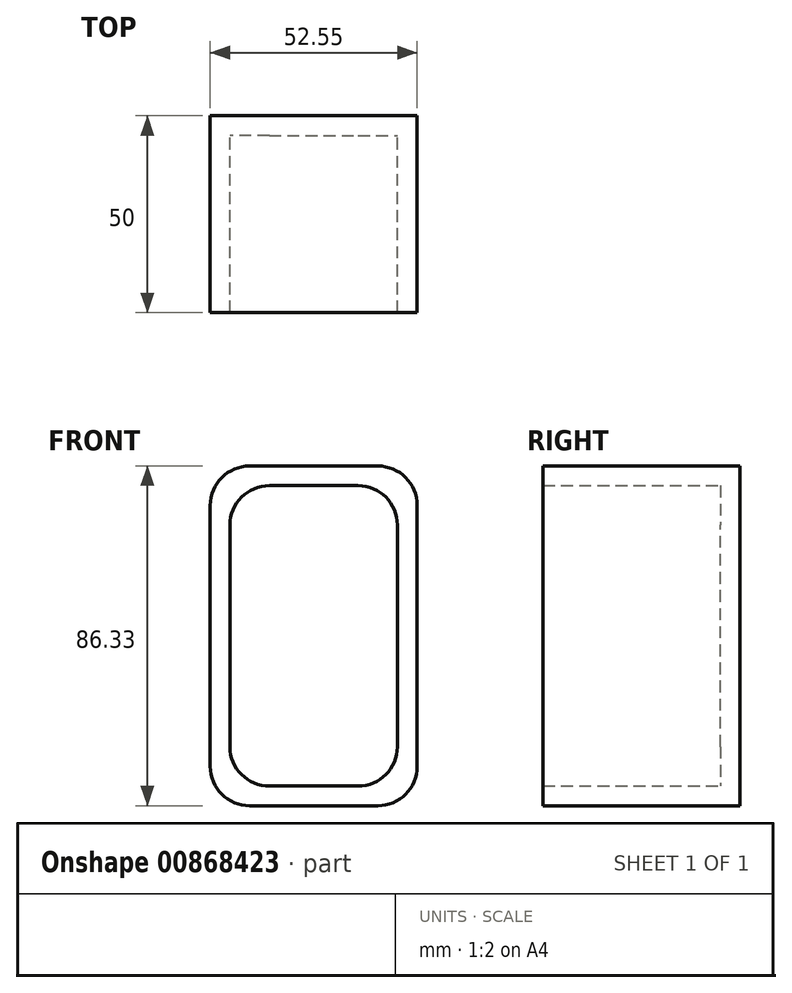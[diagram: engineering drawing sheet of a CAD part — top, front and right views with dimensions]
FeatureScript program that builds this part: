
annotation { "Feature Type Name" : "Feature", "Feature Type Description" : "" }
export const myFeature = defineFeature(function(context is Context, id is Id, definition is map)
    precondition{}
    {
        {
            var Q0;
            Q0=qCreatedBy(makeId("Front.planeOp"),FACE);
            var sketch = newSketch(context, id + "F0", { "sketchPlane" : qUnion([Q0])});
            skLineSegment(sketch, "E0.bottom", {"start": v(0, 0) * mm, "end": v(52.55, 0) * mm});
            skLineSegment(sketch, "E0.top", {"start": v(0, 51.33) * mm, "end": v(52.55, 51.33) * mm});
            skLineSegment(sketch, "E0.left", {"start": v(0, 0) * mm, "end": v(0, 51.33) * mm});
            skLineSegment(sketch, "E0.right", {"start": v(52.55, 0) * mm, "end": v(52.55, 51.33) * mm});
            skSolve(sketch);
        }
        {
            var Q0;
            Q0=makeQuery(id+"F0.imprint","IMPRINT",FACE,{"disambiguationData":[TD([[makeQuery(id+"F0.imprint","IMPRINT",EDGE,{"derivedFrom":sQuery(id+"F0.wireOp",EDGE,"E0.bottom")}),1.0]])]});
            extrude(context, id + "F1", {"entities" : qUnion([Q0]), "depth" : 50 * mm, "offsetDistance" : 25 * mm});
        }
        {
            var Q0;
            Q0=makeQuery(id+"F1.opExtrude","SWEPT_FACE",FACE,{"disambiguationData":[OSD([sQuery(id+"F0.wireOp",EDGE,"E0.top")])]});
            extrude(context, id + "F2", {"entities" : qUnion([Q0]), "operationType" : NewBodyOperationType.ADD, "depth" : 35 * mm, "offsetDistance" : 25 * mm});
        }
        {
            var Q0;
            {var subQ0=sQuery(id+"F0.wireOp",EDGE,"E0.top");Q0=makeQuery(id+"F2.boolean.opBoolean","MERGE",FACE,{"derivedFrom":[makeQuery(id+"F1.opExtrude","CAP_FACE",FACE,{"disambiguationData":[OSD([sQuery(id+"F0.wireOp",EDGE,"E0.bottom"),subQ0,sQuery(id+"F0.wireOp",EDGE,"E0.left"),sQuery(id+"F0.wireOp",EDGE,"E0.right")])],"isStart":false}),makeQuery(id+"F2.opExtrude","SWEPT_FACE",FACE,{"disambiguationData":[OSD([subQ0]),TDD([makeQuery(id+"F1.opExtrude","CAP_EDGE",EDGE,{"disambiguationData":[OSD([subQ0])],"isStart":false})])]})]});}
            shell(context, id + "F3", {"entities" : qUnion([Q0]), "thickness" : 5 * mm});
        }
        {
            var Q0;
            Q0=makeQuery(id+"F1.opExtrude","SWEPT_EDGE",EDGE,{"disambiguationData":[OSD([sQuery(id+"F0.wireOp",EDGE,"E0.bottom"),sQuery(id+"F0.wireOp",EDGE,"E0.left")])]});
            var Q1;
            Q1=makeQuery(id+"F1.opExtrude","SWEPT_EDGE",EDGE,{"disambiguationData":[OSD([sQuery(id+"F0.wireOp",EDGE,"E0.bottom"),sQuery(id+"F0.wireOp",EDGE,"E0.right")])]});
            var Q2;
            Q2=makeQuery(id+"F2.opExtrude","CAP_EDGE",EDGE,{"disambiguationData":[OSD([sQuery(id+"F0.wireOp",EDGE,"E0.top"),sQuery(id+"F0.wireOp",EDGE,"E0.left")])],"isStart":false});
            var Q3;
            Q3=makeQuery(id+"F2.opExtrude","CAP_EDGE",EDGE,{"disambiguationData":[OSD([sQuery(id+"F0.wireOp",EDGE,"E0.top"),sQuery(id+"F0.wireOp",EDGE,"E0.right")])],"isStart":false});
            fillet(context, id + "F4", {"entities" : qUnion([Q0, Q1, Q2, Q3]), "radius" : 10 * mm, "tangentPropagation" : true, "allowEdgeOverflow" : false});
        }
        {
            var Q0;
            Q0=makeQuery(id+"F3.opShell","OFFSET_EDGE",EDGE,{"disambiguationData":[OSD([sQuery(id+"F0.wireOp",EDGE,"E0.bottom"),sQuery(id+"F0.wireOp",EDGE,"E0.left")])]});
            var Q1;
            Q1=makeQuery(id+"F3.opShell","OFFSET_EDGE",EDGE,{"disambiguationData":[OSD([sQuery(id+"F0.wireOp",EDGE,"E0.bottom"),sQuery(id+"F0.wireOp",EDGE,"E0.right")])]});
            var Q2;
            {var subQ0=sQuery(id+"F0.wireOp",EDGE,"E0.right");var subQ1=sQuery(id+"F0.wireOp",EDGE,"E0.top");Q2=makeQuery(id+"F3.opShell","OFFSET_EDGE",EDGE,{"disambiguationData":[OSD([subQ1,subQ0]),TDD([makeQuery(id+"F2.opExtrude","CAP_EDGE",EDGE,{"disambiguationData":[OSD([subQ1,subQ0])],"isStart":false})])]});}
            var Q3;
            {var subQ0=sQuery(id+"F0.wireOp",EDGE,"E0.left");var subQ1=sQuery(id+"F0.wireOp",EDGE,"E0.top");Q3=makeQuery(id+"F3.opShell","OFFSET_EDGE",EDGE,{"disambiguationData":[OSD([subQ1,subQ0]),TDD([makeQuery(id+"F2.opExtrude","CAP_EDGE",EDGE,{"disambiguationData":[OSD([subQ1,subQ0])],"isStart":false})])]});}
            fillet(context, id + "F5", {"entities" : qUnion([Q0, Q1, Q2, Q3]), "radius" : 10 * mm, "tangentPropagation" : true, "allowEdgeOverflow" : false});
        }
    });
